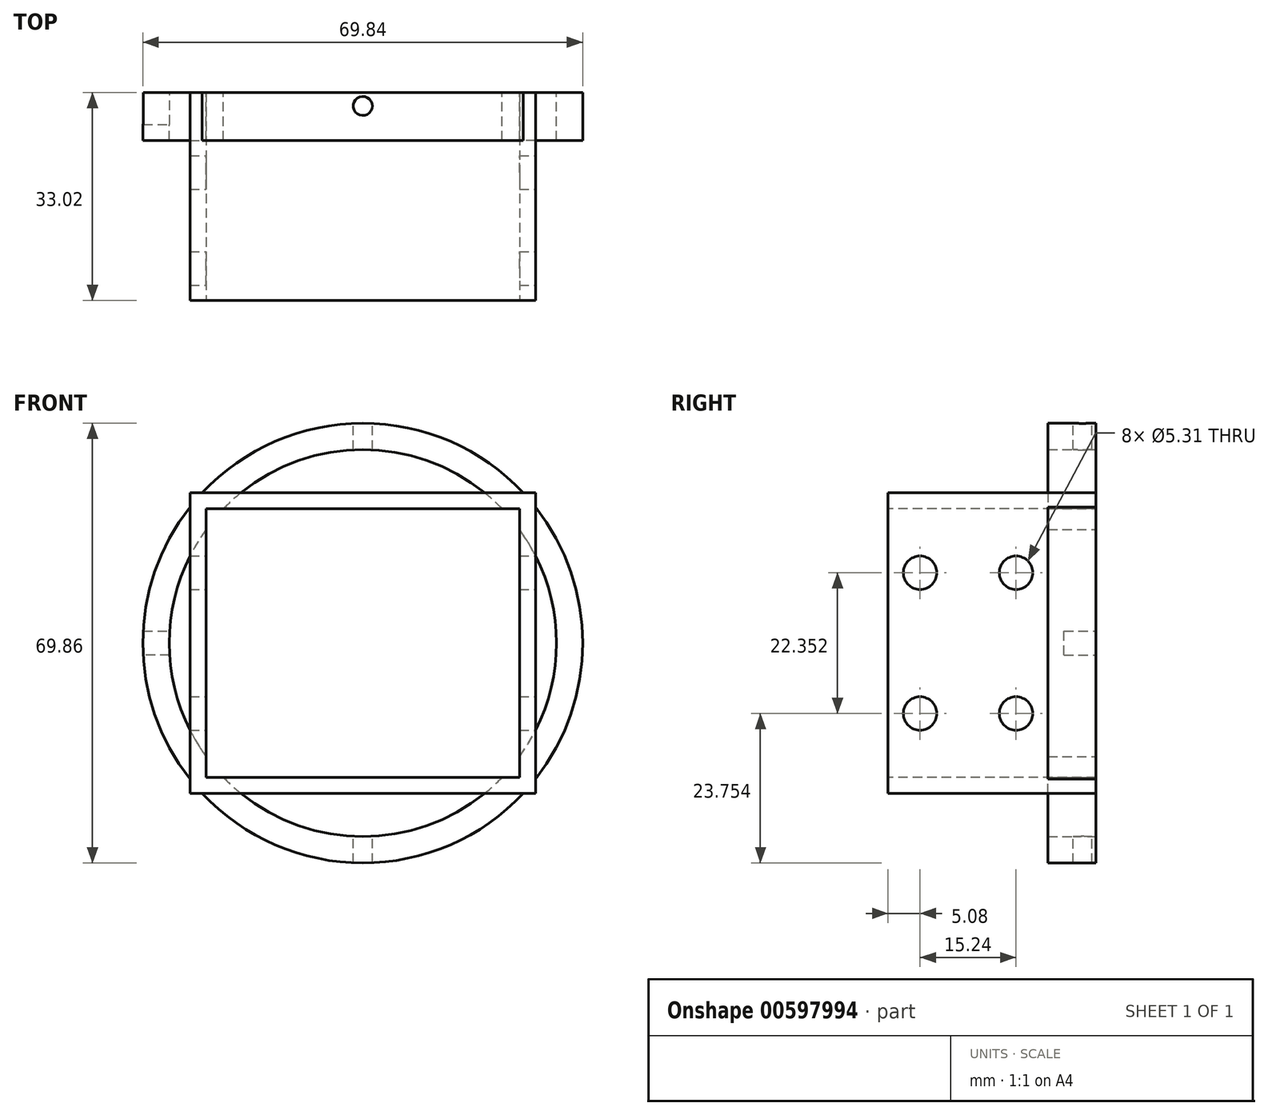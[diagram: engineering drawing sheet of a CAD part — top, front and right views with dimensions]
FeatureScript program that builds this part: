
annotation { "Feature Type Name" : "Feature", "Feature Type Description" : "" }
export const myFeature = defineFeature(function(context is Context, id is Id, definition is map)
    precondition{}
    {
        {
            var Q0;
            Q0=qCreatedBy(makeId("Front.planeOp"),FACE);
            var sketch = newSketch(context, id + "F0", { "sketchPlane" : qUnion([Q0])});
            skLineSegment(sketch, "E0.bottom", {"start": v(-27.43, 23.88) * mm, "end": v(27.43, 23.88) * mm});
            skLineSegment(sketch, "E0.top", {"start": v(-27.43, -23.88) * mm, "end": v(27.43, -23.88) * mm});
            skLineSegment(sketch, "E0.left", {"start": v(-27.43, 23.88) * mm, "end": v(-27.43, -23.88) * mm});
            skLineSegment(sketch, "E0.right", {"start": v(27.43, 23.88) * mm, "end": v(27.43, -23.88) * mm});
            skPoint(sketch, "E0.middle", {"position": v(0, 0) * mm});
            skSolve(sketch);
        }
        {
            var Q0;
            Q0=qSketchRegion(id+"F0",true);
            extrude(context, id + "F1", {"entities" : qUnion([Q0]), "depth" : 33.02 * mm, "offsetDistance" : 25.4 * mm});
        }
        {
            var Q0;
            Q0=makeQuery(id+"F1.opExtrude","CAP_FACE",FACE,{"disambiguationData":[OSD([sQuery(id+"F0.wireOp",EDGE,"E0.bottom"),sQuery(id+"F0.wireOp",EDGE,"E0.top"),sQuery(id+"F0.wireOp",EDGE,"E0.left"),sQuery(id+"F0.wireOp",EDGE,"E0.right")])],"isStart":false});
            var sketch = newSketch(context, id + "F2", { "sketchPlane" : qUnion([Q0])});
            skLineSegment(sketch, "E1", {"start": v(0, 0) * mm, "end": v(0, 21.34) * mm});
            skLineSegment(sketch, "E2", {"start": v(0, 0) * mm, "end": v(0, -21.34) * mm});
            skLineSegment(sketch, "E3", {"start": v(0, 0) * mm, "end": v(-24.9, 0) * mm});
            skLineSegment(sketch, "E4", {"start": v(0, 0) * mm, "end": v(24.9, 0) * mm});
            skLineSegment(sketch, "E5", {"start": v(-24.9, 0) * mm, "end": v(-24.9, 21.34) * mm});
            skLineSegment(sketch, "E6", {"start": v(-24.9, 21.34) * mm, "end": v(0, 21.34) * mm});
            skLineSegment(sketch, "E7", {"start": v(0, 21.34) * mm, "end": v(24.9, 21.34) * mm});
            skLineSegment(sketch, "E8", {"start": v(24.9, 21.34) * mm, "end": v(24.9, 0) * mm});
            skLineSegment(sketch, "E9", {"start": v(24.9, 0) * mm, "end": v(24.9, -21.34) * mm});
            skLineSegment(sketch, "E10", {"start": v(24.9, -21.34) * mm, "end": v(0, -21.34) * mm});
            skLineSegment(sketch, "E11", {"start": v(0, -21.34) * mm, "end": v(-24.9, -21.34) * mm});
            skLineSegment(sketch, "E12", {"start": v(-24.9, -21.34) * mm, "end": v(-24.9, 0) * mm});
            skSolve(sketch);
        }
        {
            var Q0;
            Q0=qSketchRegion(id+"F2",true);
            extrude(context, id + "F3", {"entities" : qUnion([Q0]), "operationType" : NewBodyOperationType.REMOVE, "oppositeDirection" : true, "depth" : 33.02 * mm, "offsetDistance" : 25.4 * mm});
        }
        {
            var Q0;
            Q0=makeQuery(id+"F1.opExtrude","CAP_FACE",FACE,{"disambiguationData":[OSD([sQuery(id+"F0.wireOp",EDGE,"E0.bottom"),sQuery(id+"F0.wireOp",EDGE,"E0.top"),sQuery(id+"F0.wireOp",EDGE,"E0.left"),sQuery(id+"F0.wireOp",EDGE,"E0.right")])],"isStart":true});
            var sketch = newSketch(context, id + "F4", { "sketchPlane" : qUnion([Q0])});
            skCircle(sketch, "E13", {"center": v(0, 0) * mm, "radius": 30.73 * mm});
            skCircle(sketch, "E14", {"center": v(0, 0) * mm, "radius": 34.93 * mm});
            skSolve(sketch);
        }
        {
            var Q0;
            Q0=qSketchRegion(id+"F4",true);
            extrude(context, id + "F5", {"entities" : qUnion([Q0]), "operationType" : NewBodyOperationType.ADD, "depth" : -7.62 * mm, "offsetDistance" : 25.4 * mm});
        }
        {
            var Q0;
            Q0=makeQuery(id+"F1.opExtrude","SWEPT_FACE",FACE,{"disambiguationData":[OSD([sQuery(id+"F0.wireOp",EDGE,"E0.right")])]});
            var sketch = newSketch(context, id + "F6", { "sketchPlane" : qUnion([Q0])});
            skCircle(sketch, "E15", {"center": v(-27.94, 11.18) * mm, "radius": 2.65 * mm});
            skCircle(sketch, "E16.0.1.0", {"center": v(-27.94, -11.18) * mm, "radius": 2.65 * mm});
            skCircle(sketch, "E16.1.0.0", {"center": v(-12.7, 11.18) * mm, "radius": 2.65 * mm});
            skCircle(sketch, "E16.1.1.0", {"center": v(-12.7, -11.18) * mm, "radius": 2.65 * mm});
            skLineSegment(sketch, "E16.direction1", {"start": v(-27.94, 11.18) * mm, "end": v(-12.7, 11.18) * mm, "construction": true});
            skLineSegment(sketch, "E16.direction2", {"start": v(-27.94, 11.18) * mm, "end": v(-27.94, -11.18) * mm, "construction": true});
            skSolve(sketch);
        }
        {
            var Q0;
            Q0=qSketchRegion(id+"F6",true);
            extrude(context, id + "F7", {"entities" : qUnion([Q0]), "operationType" : NewBodyOperationType.REMOVE, "oppositeDirection" : true, "depth" : 76.2 * mm, "offsetDistance" : 25.4 * mm});
        }
        {
            var Q0;
            Q0=makeQuery(id+"F5.boolean.opBoolean","MERGE",FACE,{"derivedFrom":[makeQuery(id+"F1.opExtrude","CAP_FACE",FACE,{"disambiguationData":[OSD([sQuery(id+"F0.wireOp",EDGE,"E0.bottom"),sQuery(id+"F0.wireOp",EDGE,"E0.top"),sQuery(id+"F0.wireOp",EDGE,"E0.left"),sQuery(id+"F0.wireOp",EDGE,"E0.right")])],"isStart":true}),makeQuery(id+"F5.opExtrude","CAP_FACE",FACE,{"disambiguationData":[OSD([sQuery(id+"F4.wireOp",EDGE,"E13"),sQuery(id+"F4.wireOp",EDGE,"E14")])],"isStart":true})]});
            var sketch = newSketch(context, id + "F8", { "sketchPlane" : qUnion([Q0])});
            skLineSegment(sketch, "E17", {"start": v(-21.84, 22.67) * mm, "end": v(22.17, 22.67) * mm});
            skLineSegment(sketch, "E18", {"start": v(22.17, 22.67) * mm, "end": v(17.1, 27.68) * mm});
            skLineSegment(sketch, "E19", {"start": v(17.1, 27.68) * mm, "end": v(0, 33.07) * mm});
            skLineSegment(sketch, "E20", {"start": v(0, 33.07) * mm, "end": v(-15.24, 28.93) * mm});
            skLineSegment(sketch, "E21", {"start": v(-15.24, 28.93) * mm, "end": v(-21.84, 22.67) * mm});
            skLineSegment(sketch, "E22", {"start": v(-26.72, 16.84) * mm, "end": v(-26.72, -17.02) * mm});
            skLineSegment(sketch, "E23", {"start": v(-26.72, -17.02) * mm, "end": v(-33.18, -3.64) * mm});
            skLineSegment(sketch, "E24", {"start": v(-33.18, -3.64) * mm, "end": v(-31.69, 8.96) * mm});
            skLineSegment(sketch, "E25", {"start": v(-31.69, 8.96) * mm, "end": v(-26.72, 16.84) * mm});
            skLineSegment(sketch, "E26", {"start": v(0, -33.05) * mm, "end": v(-18.06, -29.9) * mm});
            skLineSegment(sketch, "E27", {"start": v(-18.06, -29.9) * mm, "end": v(-24.9, -22.47) * mm});
            skLineSegment(sketch, "E28", {"start": v(-24.9, -22.47) * mm, "end": v(22.12, -22.47) * mm});
            skLineSegment(sketch, "E29", {"start": v(22.12, -22.47) * mm, "end": v(13.16, -30.94) * mm});
            skLineSegment(sketch, "E30", {"start": v(13.16, -30.94) * mm, "end": v(0, -33.05) * mm});
            skLineSegment(sketch, "E31", {"start": v(26.67, -17.99) * mm, "end": v(26.67, 16.76) * mm});
            skLineSegment(sketch, "E32", {"start": v(26.67, 16.76) * mm, "end": v(32.7, 5.72) * mm});
            skLineSegment(sketch, "E33", {"start": v(32.7, 5.72) * mm, "end": v(32.7, -7.18) * mm});
            skLineSegment(sketch, "E34", {"start": v(32.7, -7.18) * mm, "end": v(26.67, -17.99) * mm});
            skSolve(sketch);
        }
        {
            var Q0;
            Q0=qSketchRegion(id+"F8",true);
            extrude(context, id + "F9", {"entities" : qUnion([Q0]), "operationType" : NewBodyOperationType.ADD, "depth" : -7.62 * mm, "offsetDistance" : 25.4 * mm});
        }
        {
            var Q0;
            Q0=makeQuery(id+"F9.boolean.opBoolean","MERGE",FACE,{"derivedFrom":[makeQuery(id+"F5.boolean.opBoolean","MERGE",FACE,{"derivedFrom":[makeQuery(id+"F1.opExtrude","CAP_FACE",FACE,{"disambiguationData":[OSD([sQuery(id+"F0.wireOp",EDGE,"E0.bottom"),sQuery(id+"F0.wireOp",EDGE,"E0.top"),sQuery(id+"F0.wireOp",EDGE,"E0.left"),sQuery(id+"F0.wireOp",EDGE,"E0.right")])],"isStart":true}),makeQuery(id+"F5.opExtrude","CAP_FACE",FACE,{"disambiguationData":[OSD([sQuery(id+"F4.wireOp",EDGE,"E13"),sQuery(id+"F4.wireOp",EDGE,"E14")])],"isStart":true})]}),makeQuery(id+"F9.opExtrude","CAP_FACE",FACE,{"disambiguationData":[OSD([sQuery(id+"F8.wireOp",EDGE,"E17"),sQuery(id+"F8.wireOp",EDGE,"E18"),sQuery(id+"F8.wireOp",EDGE,"E19"),sQuery(id+"F8.wireOp",EDGE,"E20"),sQuery(id+"F8.wireOp",EDGE,"E21")])],"isStart":true}),makeQuery(id+"F9.opExtrude","CAP_FACE",FACE,{"disambiguationData":[OSD([sQuery(id+"F8.wireOp",EDGE,"E22"),sQuery(id+"F8.wireOp",EDGE,"E23"),sQuery(id+"F8.wireOp",EDGE,"E24"),sQuery(id+"F8.wireOp",EDGE,"E25")])],"isStart":true}),makeQuery(id+"F9.opExtrude","CAP_FACE",FACE,{"disambiguationData":[OSD([sQuery(id+"F8.wireOp",EDGE,"E26"),sQuery(id+"F8.wireOp",EDGE,"E27"),sQuery(id+"F8.wireOp",EDGE,"E28"),sQuery(id+"F8.wireOp",EDGE,"E29"),sQuery(id+"F8.wireOp",EDGE,"E30")])],"isStart":true}),makeQuery(id+"F9.opExtrude","CAP_FACE",FACE,{"disambiguationData":[OSD([sQuery(id+"F8.wireOp",EDGE,"E31"),sQuery(id+"F8.wireOp",EDGE,"E32"),sQuery(id+"F8.wireOp",EDGE,"E33"),sQuery(id+"F8.wireOp",EDGE,"E34")])],"isStart":true})]});
            var sketch = newSketch(context, id + "F10", { "sketchPlane" : qUnion([Q0])});
            skLineSegment(sketch, "E35", {"start": v(-22.12, 21.34) * mm, "end": v(-24.9, 21.34) * mm});
            skLineSegment(sketch, "E36", {"start": v(-24.9, 21.34) * mm, "end": v(-24.9, -18.03) * mm});
            skLineSegment(sketch, "E37", {"start": v(-24.9, -18.03) * mm, "end": v(-24.9, -21.34) * mm});
            skLineSegment(sketch, "E38", {"start": v(-24.9, -21.34) * mm, "end": v(24.9, -21.34) * mm});
            skLineSegment(sketch, "E39", {"start": v(24.9, -21.34) * mm, "end": v(24.9, 21.34) * mm});
            skLineSegment(sketch, "E40", {"start": v(24.9, 21.34) * mm, "end": v(-22.12, 21.34) * mm});
            skSolve(sketch);
        }
        {
            var Q0;
            Q0=qSketchRegion(id+"F10",true);
            extrude(context, id + "F11", {"entities" : qUnion([Q0]), "operationType" : NewBodyOperationType.REMOVE, "oppositeDirection" : true, "depth" : 25.4 * mm, "offsetDistance" : 25.4 * mm});
        }
        {
            var Q0;
            Q0=makeQuery(id+"F9.boolean.opBoolean","MERGE",FACE,{"derivedFrom":[makeQuery(id+"F5.boolean.opBoolean","MERGE",FACE,{"derivedFrom":[makeQuery(id+"F1.opExtrude","CAP_FACE",FACE,{"disambiguationData":[OSD([sQuery(id+"F0.wireOp",EDGE,"E0.bottom"),sQuery(id+"F0.wireOp",EDGE,"E0.top"),sQuery(id+"F0.wireOp",EDGE,"E0.left"),sQuery(id+"F0.wireOp",EDGE,"E0.right")])],"isStart":true}),makeQuery(id+"F5.opExtrude","CAP_FACE",FACE,{"disambiguationData":[OSD([sQuery(id+"F4.wireOp",EDGE,"E13"),sQuery(id+"F4.wireOp",EDGE,"E14")])],"isStart":true})]}),makeQuery(id+"F9.opExtrude","CAP_FACE",FACE,{"disambiguationData":[OSD([sQuery(id+"F8.wireOp",EDGE,"E17"),sQuery(id+"F8.wireOp",EDGE,"E18"),sQuery(id+"F8.wireOp",EDGE,"E19"),sQuery(id+"F8.wireOp",EDGE,"E20"),sQuery(id+"F8.wireOp",EDGE,"E21")])],"isStart":true}),makeQuery(id+"F9.opExtrude","CAP_FACE",FACE,{"disambiguationData":[OSD([sQuery(id+"F8.wireOp",EDGE,"E22"),sQuery(id+"F8.wireOp",EDGE,"E23"),sQuery(id+"F8.wireOp",EDGE,"E24"),sQuery(id+"F8.wireOp",EDGE,"E25")])],"isStart":true}),makeQuery(id+"F9.opExtrude","CAP_FACE",FACE,{"disambiguationData":[OSD([sQuery(id+"F8.wireOp",EDGE,"E26"),sQuery(id+"F8.wireOp",EDGE,"E27"),sQuery(id+"F8.wireOp",EDGE,"E28"),sQuery(id+"F8.wireOp",EDGE,"E29"),sQuery(id+"F8.wireOp",EDGE,"E30")])],"isStart":true}),makeQuery(id+"F9.opExtrude","CAP_FACE",FACE,{"disambiguationData":[OSD([sQuery(id+"F8.wireOp",EDGE,"E31"),sQuery(id+"F8.wireOp",EDGE,"E32"),sQuery(id+"F8.wireOp",EDGE,"E33"),sQuery(id+"F8.wireOp",EDGE,"E34")])],"isStart":true})]});
            var sketch = newSketch(context, id + "F12", { "sketchPlane" : qUnion([Q0])});
            skCircle(sketch, "E41", {"center": v(0, 0) * mm, "radius": 30.73 * mm});
            skSolve(sketch);
        }
        {
            var Q0;
            Q0=qSketchRegion(id+"F12",true);
            extrude(context, id + "F13", {"entities" : qUnion([Q0]), "operationType" : NewBodyOperationType.REMOVE, "oppositeDirection" : true, "depth" : 7.62 * mm, "offsetDistance" : 25.4 * mm});
        }
        {
            var Q0;
            Q0=makeQuery(id+"F9.boolean.opBoolean","MERGE",FACE,{"derivedFrom":[makeQuery(id+"F5.boolean.opBoolean","MERGE",FACE,{"derivedFrom":[makeQuery(id+"F1.opExtrude","CAP_FACE",FACE,{"disambiguationData":[OSD([sQuery(id+"F0.wireOp",EDGE,"E0.bottom"),sQuery(id+"F0.wireOp",EDGE,"E0.top"),sQuery(id+"F0.wireOp",EDGE,"E0.left"),sQuery(id+"F0.wireOp",EDGE,"E0.right")])],"isStart":true}),makeQuery(id+"F5.opExtrude","CAP_FACE",FACE,{"disambiguationData":[OSD([sQuery(id+"F4.wireOp",EDGE,"E13"),sQuery(id+"F4.wireOp",EDGE,"E14")])],"isStart":true})]}),makeQuery(id+"F9.opExtrude","CAP_FACE",FACE,{"disambiguationData":[OSD([sQuery(id+"F8.wireOp",EDGE,"E17"),sQuery(id+"F8.wireOp",EDGE,"E18"),sQuery(id+"F8.wireOp",EDGE,"E19"),sQuery(id+"F8.wireOp",EDGE,"E20"),sQuery(id+"F8.wireOp",EDGE,"E21")])],"isStart":true}),makeQuery(id+"F9.opExtrude","CAP_FACE",FACE,{"disambiguationData":[OSD([sQuery(id+"F8.wireOp",EDGE,"E22"),sQuery(id+"F8.wireOp",EDGE,"E23"),sQuery(id+"F8.wireOp",EDGE,"E24"),sQuery(id+"F8.wireOp",EDGE,"E25")])],"isStart":true}),makeQuery(id+"F9.opExtrude","CAP_FACE",FACE,{"disambiguationData":[OSD([sQuery(id+"F8.wireOp",EDGE,"E26"),sQuery(id+"F8.wireOp",EDGE,"E27"),sQuery(id+"F8.wireOp",EDGE,"E28"),sQuery(id+"F8.wireOp",EDGE,"E29"),sQuery(id+"F8.wireOp",EDGE,"E30")])],"isStart":true}),makeQuery(id+"F9.opExtrude","CAP_FACE",FACE,{"disambiguationData":[OSD([sQuery(id+"F8.wireOp",EDGE,"E31"),sQuery(id+"F8.wireOp",EDGE,"E32"),sQuery(id+"F8.wireOp",EDGE,"E33"),sQuery(id+"F8.wireOp",EDGE,"E34")])],"isStart":true})]});
            var sketch = newSketch(context, id + "F14", { "sketchPlane" : qUnion([Q0])});
            skLineSegment(sketch, "E42", {"start": v(30.67, 1.9) * mm, "end": v(34.87, 1.9) * mm});
            skLineSegment(sketch, "E43", {"start": v(34.87, -1.9) * mm, "end": v(30.67, -1.9) * mm});
            skLineSegment(sketch, "E44", {"start": v(34.87, 1.9) * mm, "end": v(38.5, 0.96) * mm});
            skLineSegment(sketch, "E45", {"start": v(38.5, 0.96) * mm, "end": v(34.87, -1.9) * mm});
            skLineSegment(sketch, "E46", {"start": v(30.67, 1.9) * mm, "end": v(30.03, 1.9) * mm});
            skLineSegment(sketch, "E47", {"start": v(30.03, 1.9) * mm, "end": v(29.74, -1.79) * mm});
            skLineSegment(sketch, "E48", {"start": v(29.74, -1.79) * mm, "end": v(30.5, -1.9) * mm});
            skLineSegment(sketch, "E49", {"start": v(30.5, -1.9) * mm, "end": v(30.67, -1.9) * mm});
            skSolve(sketch);
        }
        {
            var Q0;
            Q0=qSketchRegion(id+"F14",true);
            extrude(context, id + "F15", {"entities" : qUnion([Q0]), "operationType" : NewBodyOperationType.REMOVE, "oppositeDirection" : true, "depth" : 5.08 * mm, "offsetDistance" : 25.4 * mm});
        }
        {
            var Q0;
            Q0=qCreatedBy(makeId("Top.planeOp"),FACE);
            cPlane(context, id + "F16", {"entities" : qUnion([Q0]), "cplaneType" : CPlaneType.OFFSET, "offset" : 76.2 * mm, "width" : 152.4 * mm, "height" : 152.4 * mm});
        }
        {
            var Q0;
            Q0=qCreatedBy(id+"F16.planeOp",FACE);
            var sketch = newSketch(context, id + "F17", { "sketchPlane" : qUnion([Q0])});
            skCircle(sketch, "E50", {"center": v(0, -2.15) * mm, "radius": 1.51 * mm});
            skSolve(sketch);
        }
        {
            var Q0;
            Q0=qSketchRegion(id+"F17",true);
            extrude(context, id + "F18", {"entities" : qUnion([Q0]), "operationType" : NewBodyOperationType.REMOVE, "oppositeDirection" : true, "depth" : 127 * mm, "offsetDistance" : 25.4 * mm});
        }
    });
